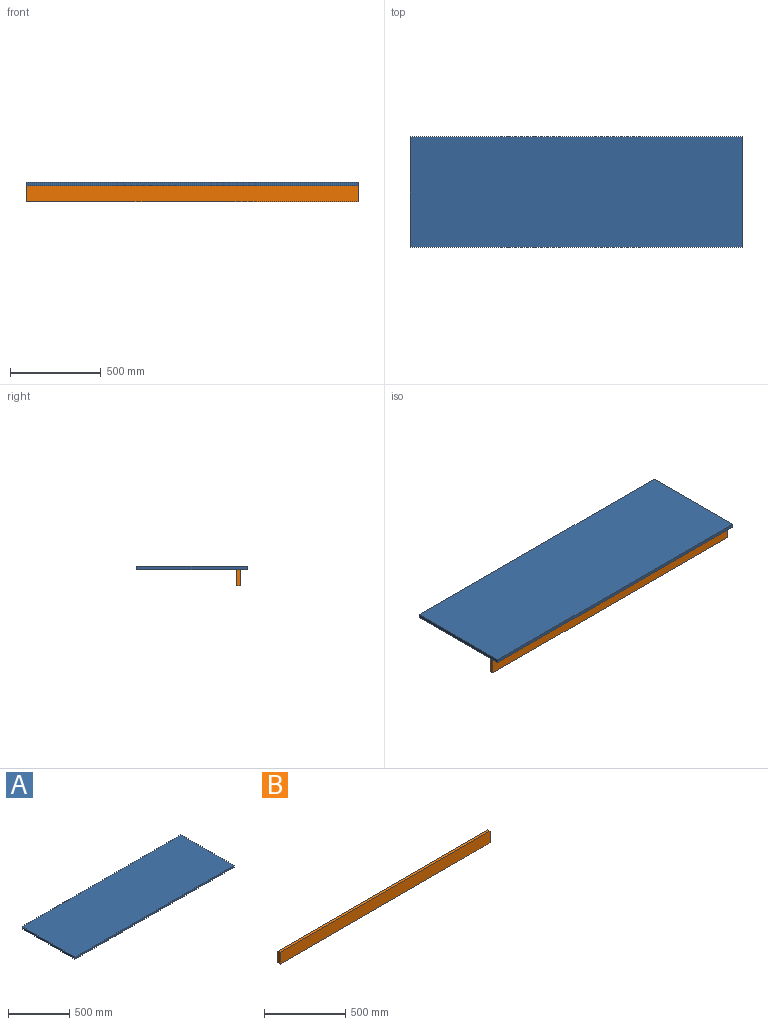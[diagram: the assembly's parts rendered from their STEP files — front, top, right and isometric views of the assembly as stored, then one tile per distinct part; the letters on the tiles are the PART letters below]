
ASSEMBLY  parts=2 mates=2
PART A: 6 faces, bbox 1828.8x609.6x19.1 mm
  f0: plane 1828.8x19.05mm, normal (0,1,0), area 34838.6mm2, adj f1,f3,f4,f5
  f1: plane 609.6x19.05mm, normal (-1,0,0), area 11612.9mm2, adj f0,f2,f4,f5
  f2: plane 1828.8x19.05mm, normal (0,-1,0), area 34838.6mm2, adj f1,f3,f4,f5
  f3: plane 609.6x19.05mm, normal (1,0,0), area 11612.9mm2, adj f0,f2,f4,f5
  f4: plane 1828.8x609.6mm, normal (0,0,1), area 1114836.5mm2, adj f0,f1,f2,f3
  f5: plane 1828.8x609.6mm, normal (0,0,-1), area 1114836.5mm2, adj f0,f1,f2,f3
PART B: 6 faces, bbox 1828.8x19.1x88.9 mm
  f0: plane 1828.8x19.05mm, normal (0,0,1), area 34838.6mm2, adj f1,f3,f4,f5
  f1: plane 88.9x19.05mm, normal (-1,0,0), area 1693.5mm2, adj f0,f2,f4,f5
  f2: plane 1828.8x19.05mm, normal (0,0,-1), area 34838.6mm2, adj f1,f3,f4,f5
  f3: plane 88.9x19.05mm, normal (1,0,0), area 1693.5mm2, adj f0,f2,f4,f5
  f4: plane 1828.8x88.9mm, normal (0,-1,0), area 162580.3mm2, adj f0,f1,f2,f3
  f5: plane 1828.8x88.9mm, normal (0,1,0), area 162580.3mm2, adj f0,f1,f2,f3
PLACE A t=(12.18,-1.95,-54.92)mm
PLACE B t=(12.18,-248.94,-99.37)mm
MATE planar B.f0 <-> A.f5  axis (0,0,1) through (12.18,-258.47,-54.92)mm
MATE planar B.f1 <-> A.f1  axis (-1,0,0) through (-902.22,-258.47,-99.37)mm
